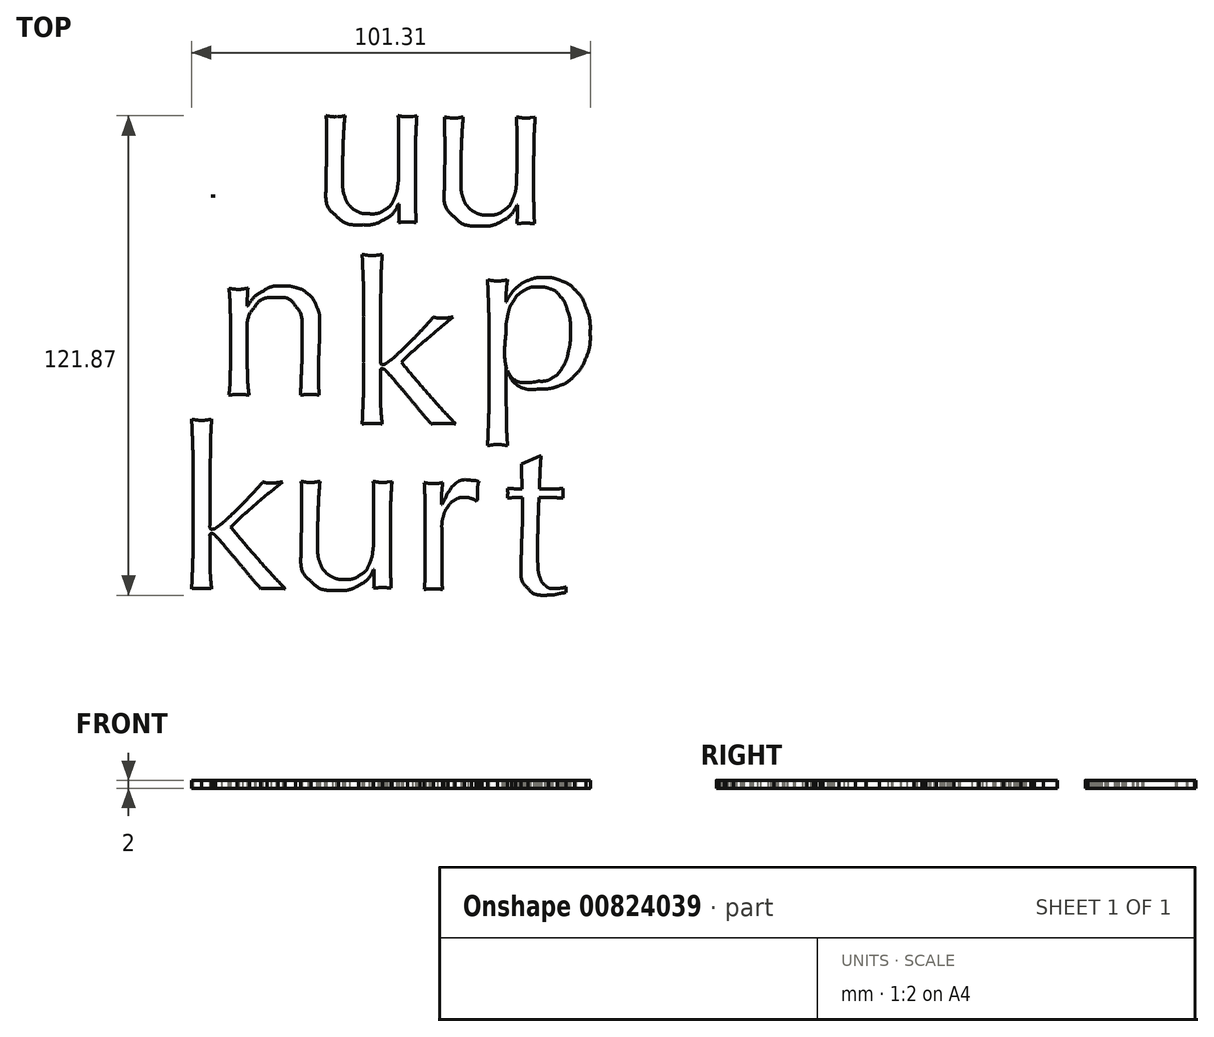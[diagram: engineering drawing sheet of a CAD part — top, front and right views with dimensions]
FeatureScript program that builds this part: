
annotation { "Feature Type Name" : "Feature", "Feature Type Description" : "" }
export const myFeature = defineFeature(function(context is Context, id is Id, definition is map)
    precondition{}
    {
        {
            var Q0;
            Q0=qCreatedBy(makeId("Top.planeOp"),FACE);
            var sketch = newSketch(context, id + "F0", { "sketchPlane" : qUnion([Q0])});
            skFitSpline(sketch, "E0", {"points": [v(-42.87, 37.01) * mm, v(-41.88, 37.01) * mm, v(-40.85, 37) * mm, v(-39.78, 36.95) * mm]});
            skFitSpline(sketch, "E1", {"points": [v(-39.78, 36.95) * mm, v(-38.71, 36.91) * mm, v(-37.69, 36.9) * mm, v(-36.7, 36.9) * mm]});
            skFitSpline(sketch, "E2", {"points": [v(-36.7, 36.9) * mm, v(-35.63, 36.9) * mm, v(-34.56, 36.9) * mm, v(-33.5, 36.9) * mm]});
            skFitSpline(sketch, "E3", {"points": [v(-33.5, 36.9) * mm, v(-32.43, 36.93) * mm, v(-31.36, 36.97) * mm, v(-30.3, 37.01) * mm]});
            skFitSpline(sketch, "E4", {"points": [v(-17.55, 19.24) * mm, v(-18.09, 19.31) * mm, v(-18.6, 19.35) * mm, v(-19.1, 19.35) * mm]});
            skFitSpline(sketch, "E5", {"points": [v(-19.1, 19.35) * mm, v(-19.55, 19.35) * mm, v(-20.05, 19.35) * mm, v(-20.58, 19.35) * mm]});
            skFitSpline(sketch, "E6", {"points": [v(-20.58, 19.35) * mm, v(-21.11, 19.35) * mm, v(-21.63, 19.35) * mm, v(-22.12, 19.35) * mm]});
            skFitSpline(sketch, "E7", {"points": [v(-22.12, 19.35) * mm, v(-22.58, 19.35) * mm, v(-23.08, 19.31) * mm, v(-23.6, 19.24) * mm]});
            skFitSpline(sketch, "E8", {"points": [v(-23.6, 19.24) * mm, v(-23.88, 20.11) * mm, v(-24.24, 21.16) * mm, v(-24.7, 22.38) * mm]});
            skFitSpline(sketch, "E9", {"points": [v(-24.7, 22.38) * mm, v(-25.15, 23.64) * mm, v(-25.67, 24.93) * mm, v(-26.24, 26.27) * mm]});
            skFitSpline(sketch, "E10", {"points": [v(-26.24, 26.27) * mm, v(-26.77, 27.64) * mm, v(-27.32, 29.01) * mm, v(-27.9, 30.38) * mm]});
            skFitSpline(sketch, "E11", {"points": [v(-27.9, 30.38) * mm, v(-28.47, 31.8) * mm, v(-29, 33.12) * mm, v(-29.5, 34.38) * mm]});
            skFitSpline(sketch, "E12", {"points": [v(-29.5, 34.38) * mm, v(-30.71, 34.42) * mm, v(-31.95, 34.44) * mm, v(-33.2, 34.44) * mm]});
            skFitSpline(sketch, "E13", {"points": [v(-33.2, 34.44) * mm, v(-34.47, 34.48) * mm, v(-35.72, 34.5) * mm, v(-36.98, 34.5) * mm]});
            skFitSpline(sketch, "E14", {"points": [v(-36.98, 34.5) * mm, v(-38.16, 34.5) * mm, v(-39.32, 34.48) * mm, v(-40.47, 34.44) * mm]});
            skFitSpline(sketch, "E15", {"points": [v(-40.47, 34.44) * mm, v(-41.6, 34.44) * mm, v(-42.77, 34.42) * mm, v(-43.95, 34.38) * mm]});
            skFitSpline(sketch, "E16", {"points": [v(-43.95, 34.38) * mm, v(-45.17, 31.41) * mm, v(-46.28, 28.57) * mm, v(-47.27, 25.87) * mm]});
            skFitSpline(sketch, "E17", {"points": [v(-47.27, 25.87) * mm, v(-48.26, 23.2) * mm, v(-49, 21) * mm, v(-49.5, 19.24) * mm]});
            skFitSpline(sketch, "E18", {"points": [v(-49.5, 19.24) * mm, v(-50.14, 19.31) * mm, v(-50.85, 19.35) * mm, v(-51.6, 19.35) * mm]});
            skFitSpline(sketch, "E19", {"points": [v(-51.6, 19.35) * mm, v(-52.37, 19.35) * mm, v(-53.08, 19.31) * mm, v(-53.72, 19.24) * mm]});
            skFitSpline(sketch, "E20", {"points": [v(-53.72, 19.24) * mm, v(-50.64, 25.9) * mm, v(-47.63, 32.53) * mm, v(-44.7, 39.12) * mm]});
            skFitSpline(sketch, "E21", {"points": [v(-44.7, 39.12) * mm, v(-41.76, 45.71) * mm, v(-38.8, 52.42) * mm, v(-35.84, 59.24) * mm]});
            skLineSegment(sketch, "E22", {"start": v(-30.3, 37.01) * mm, "end": v(-36.64, 51.52) * mm});
            skLineSegment(sketch, "E23", {"start": v(-36.64, 51.52) * mm, "end": v(-42.87, 37.01) * mm});
            skLineSegment(sketch, "E24", {"start": v(-42.87, 37.01) * mm, "end": v(-30.3, 37.01) * mm});
            skFitSpline(sketch, "E25", {"points": [v(-34.75, 59.24) * mm, v(-33.84, 57.03) * mm, v(-32.85, 54.63) * mm, v(-31.78, 52.04) * mm]});
            skFitSpline(sketch, "E26", {"points": [v(-31.78, 52.04) * mm, v(-30.71, 49.49) * mm, v(-29.63, 46.9) * mm, v(-28.52, 44.27) * mm]});
            skFitSpline(sketch, "E27", {"points": [v(-28.52, 44.27) * mm, v(-27.42, 41.64) * mm, v(-26.31, 39.03) * mm, v(-25.2, 36.44) * mm]});
            skFitSpline(sketch, "E28", {"points": [v(-25.2, 36.44) * mm, v(-24.1, 33.85) * mm, v(-23.08, 31.43) * mm, v(-22.12, 29.18) * mm]});
            skFitSpline(sketch, "E29", {"points": [v(-22.12, 29.18) * mm, v(-21.13, 26.97) * mm, v(-20.26, 25) * mm, v(-19.5, 23.24) * mm]});
            skFitSpline(sketch, "E30", {"points": [v(-19.5, 23.24) * mm, v(-18.7, 21.49) * mm, v(-18.05, 20.15) * mm, v(-17.55, 19.24) * mm]});
            skLineSegment(sketch, "E31", {"start": v(-35.84, 59.24) * mm, "end": v(-34.75, 59.24) * mm});
            skLineSegment(sketch, "E32", {"start": v(-34.75, 59.24) * mm, "end": v(-35.84, 59.24) * mm});
            skFitSpline(sketch, "E33", {"points": [v(-4.04, -4.63) * mm, v(-4.04, -5.93) * mm, v(-4.06, -7.34) * mm, v(-4.1, -8.86) * mm]});
            skFitSpline(sketch, "E34", {"points": [v(-4.1, -8.86) * mm, v(-4.1, -10.39) * mm, v(-4.12, -11.9) * mm, v(-4.16, -13.38) * mm]});
            skFitSpline(sketch, "E35", {"points": [v(-4.16, -13.38) * mm, v(-4.2, -14.86) * mm, v(-4.25, -16.27) * mm, v(-4.33, -17.6) * mm]});
            skFitSpline(sketch, "E36", {"points": [v(-4.33, -17.6) * mm, v(-4.37, -18.94) * mm, v(-4.42, -20.04) * mm, v(-4.5, -20.92) * mm]});
            skFitSpline(sketch, "E37", {"points": [v(-4.5, -20.92) * mm, v(-3.62, -20.84) * mm, v(-2.77, -20.8) * mm, v(-1.93, -20.8) * mm]});
            skFitSpline(sketch, "E38", {"points": [v(-1.93, -20.8) * mm, v(-1.09, -20.8) * mm, v(-0.23, -20.84) * mm, v(0.64, -20.92) * mm]});
            skFitSpline(sketch, "E39", {"points": [v(0.64, -20.92) * mm, v(0.45, -19.28) * mm, v(0.32, -17.66) * mm, v(0.24, -16.06) * mm]});
            skFitSpline(sketch, "E40", {"points": [v(0.24, -16.06) * mm, v(0.2, -14.42) * mm, v(0.19, -12.75) * mm, v(0.19, -11.03) * mm]});
            skLineSegment(sketch, "E41", {"start": v(-4.04, 5.7) * mm, "end": v(-4.04, -4.63) * mm});
            skLineSegment(sketch, "E42", {"start": v(-4.04, -4.63) * mm, "end": v(-4.04, 5.7) * mm});
            skFitSpline(sketch, "E43", {"points": [v(0.19, -7.6) * mm, v(0.19, -7.15) * mm, v(0.38, -6.92) * mm, v(0.76, -6.92) * mm]});
            skFitSpline(sketch, "E44", {"points": [v(0.76, -6.92) * mm, v(0.91, -6.92) * mm, v(1.06, -6.98) * mm, v(1.22, -7.1) * mm]});
            skFitSpline(sketch, "E45", {"points": [v(1.22, -7.1) * mm, v(1.37, -7.2) * mm, v(1.5, -7.34) * mm, v(1.62, -7.5) * mm]});
            skFitSpline(sketch, "E46", {"points": [v(1.62, -7.5) * mm, v(2.3, -8.21) * mm, v(3.12, -9.13) * mm, v(4.07, -10.23) * mm]});
            skFitSpline(sketch, "E47", {"points": [v(4.07, -10.23) * mm, v(5.02, -11.34) * mm, v(6.02, -12.52) * mm, v(7.04, -13.78) * mm]});
            skFitSpline(sketch, "E48", {"points": [v(7.04, -13.78) * mm, v(8.11, -15.03) * mm, v(9.18, -16.31) * mm, v(10.24, -17.6) * mm]});
            skFitSpline(sketch, "E49", {"points": [v(10.24, -17.6) * mm, v(11.31, -18.86) * mm, v(12.26, -19.97) * mm, v(13.1, -20.92) * mm]});
            skFitSpline(sketch, "E50", {"points": [v(13.1, -20.92) * mm, v(13.63, -20.84) * mm, v(14.15, -20.8) * mm, v(14.64, -20.8) * mm]});
            skFitSpline(sketch, "E51", {"points": [v(14.64, -20.8) * mm, v(15.14, -20.8) * mm, v(15.6, -20.8) * mm, v(16.02, -20.8) * mm]});
            skFitSpline(sketch, "E52", {"points": [v(16.02, -20.8) * mm, v(16.51, -20.8) * mm, v(17, -20.8) * mm, v(17.5, -20.8) * mm]});
            skFitSpline(sketch, "E53", {"points": [v(17.5, -20.8) * mm, v(18.03, -20.8) * mm, v(18.62, -20.84) * mm, v(19.27, -20.92) * mm]});
            skFitSpline(sketch, "E54", {"points": [v(19.27, -20.92) * mm, v(16.87, -18.37) * mm, v(14.51, -15.78) * mm, v(12.19, -13.15) * mm]});
            skFitSpline(sketch, "E55", {"points": [v(12.19, -13.15) * mm, v(9.9, -10.52) * mm, v(7.67, -7.9) * mm, v(5.5, -5.26) * mm]});
            skFitSpline(sketch, "E56", {"points": [v(5.5, -5.26) * mm, v(7.48, -3.32) * mm, v(9.56, -1.41) * mm, v(11.73, 0.45) * mm]});
            skFitSpline(sketch, "E57", {"points": [v(11.73, 0.45) * mm, v(13.94, 2.36) * mm, v(16.24, 4.28) * mm, v(18.64, 6.22) * mm]});
            skFitSpline(sketch, "E58", {"points": [v(18.64, 6.22) * mm, v(18, 6.15) * mm, v(17.46, 6.07) * mm, v(17.04, 6) * mm]});
            skFitSpline(sketch, "E59", {"points": [v(17.04, 6) * mm, v(16.62, 5.96) * mm, v(16.2, 5.94) * mm, v(15.79, 5.94) * mm]});
            skFitSpline(sketch, "E60", {"points": [v(15.79, 5.94) * mm, v(15.1, 5.94) * mm, v(14.38, 6.03) * mm, v(13.62, 6.22) * mm]});
            skFitSpline(sketch, "E61", {"points": [v(13.62, 6.22) * mm, v(12.74, 5.2) * mm, v(11.77, 4.1) * mm, v(10.7, 2.97) * mm]});
            skFitSpline(sketch, "E62", {"points": [v(10.7, 2.97) * mm, v(9.63, 1.82) * mm, v(8.59, 0.74) * mm, v(7.56, -0.3) * mm]});
            skFitSpline(sketch, "E63", {"points": [v(7.56, -0.3) * mm, v(6.57, -1.28) * mm, v(5.65, -2.16) * mm, v(4.82, -2.92) * mm]});
            skFitSpline(sketch, "E64", {"points": [v(4.82, -2.92) * mm, v(4.02, -3.68) * mm, v(3.44, -4.2) * mm, v(3.1, -4.46) * mm]});
            skFitSpline(sketch, "E65", {"points": [v(3.1, -4.46) * mm, v(2.64, -4.8) * mm, v(2.22, -5.11) * mm, v(1.84, -5.38) * mm]});
            skFitSpline(sketch, "E66", {"points": [v(1.84, -5.38) * mm, v(1.5, -5.64) * mm, v(1.18, -5.78) * mm, v(0.87, -5.78) * mm]});
            skFitSpline(sketch, "E67", {"points": [v(0.87, -5.78) * mm, v(0.42, -5.78) * mm, v(0.19, -5.41) * mm, v(0.19, -4.7) * mm]});
            skLineSegment(sketch, "E68", {"start": v(0.19, -11.03) * mm, "end": v(0.19, -7.6) * mm});
            skLineSegment(sketch, "E69", {"start": v(0.19, -7.6) * mm, "end": v(0.19, -11.03) * mm});
            skFitSpline(sketch, "E70", {"points": [v(0.19, 5.7) * mm, v(0.19, 7) * mm, v(0.19, 8.41) * mm, v(0.19, 9.94) * mm]});
            skFitSpline(sketch, "E71", {"points": [v(0.19, 9.94) * mm, v(0.22, 11.46) * mm, v(0.26, 12.97) * mm, v(0.3, 14.45) * mm]});
            skFitSpline(sketch, "E72", {"points": [v(0.3, 14.45) * mm, v(0.34, 15.94) * mm, v(0.38, 17.35) * mm, v(0.42, 18.68) * mm]});
            skFitSpline(sketch, "E73", {"points": [v(0.42, 18.68) * mm, v(0.5, 20.05) * mm, v(0.57, 21.21) * mm, v(0.64, 22.17) * mm]});
            skFitSpline(sketch, "E74", {"points": [v(0.64, 22.17) * mm, v(-0.42, 21.98) * mm, v(-1.28, 21.88) * mm, v(-1.93, 21.88) * mm]});
            skFitSpline(sketch, "E75", {"points": [v(-1.93, 21.88) * mm, v(-2.58, 21.88) * mm, v(-3.43, 21.98) * mm, v(-4.5, 22.17) * mm]});
            skFitSpline(sketch, "E76", {"points": [v(-4.5, 22.17) * mm, v(-4.42, 21.21) * mm, v(-4.37, 20.05) * mm, v(-4.33, 18.68) * mm]});
            skFitSpline(sketch, "E77", {"points": [v(-4.33, 18.68) * mm, v(-4.25, 17.35) * mm, v(-4.2, 15.94) * mm, v(-4.16, 14.45) * mm]});
            skFitSpline(sketch, "E78", {"points": [v(-4.16, 14.45) * mm, v(-4.12, 12.97) * mm, v(-4.1, 11.46) * mm, v(-4.1, 9.94) * mm]});
            skFitSpline(sketch, "E79", {"points": [v(-4.1, 9.94) * mm, v(-4.06, 8.41) * mm, v(-4.04, 7) * mm, v(-4.04, 5.7) * mm]});
            skLineSegment(sketch, "E80", {"start": v(0.19, -4.7) * mm, "end": v(0.19, 5.7) * mm});
            skLineSegment(sketch, "E81", {"start": v(0.19, 5.7) * mm, "end": v(0.19, -4.7) * mm});
            skFitSpline(sketch, "E82", {"points": [v(-13.65, 38.87) * mm, v(-13.65, 35.9) * mm, v(-12.8, 33.62) * mm, v(-11.13, 32.02) * mm]});
            skFitSpline(sketch, "E83", {"points": [v(-11.13, 32.02) * mm, v(-9.42, 30.46) * mm, v(-7.07, 29.67) * mm, v(-4.1, 29.67) * mm]});
            skFitSpline(sketch, "E84", {"points": [v(-4.1, 29.67) * mm, v(-2.27, 29.67) * mm, v(-0.58, 30.1) * mm, v(0.98, 30.93) * mm]});
            skFitSpline(sketch, "E85", {"points": [v(0.98, 30.93) * mm, v(2.55, 31.8) * mm, v(3.82, 33.16) * mm, v(4.81, 34.99) * mm]});
            skFitSpline(sketch, "E86", {"points": [v(4.93, 32.53) * mm, v(4.93, 32.11) * mm, v(4.9, 31.71) * mm, v(4.87, 31.33) * mm]});
            skFitSpline(sketch, "E87", {"points": [v(4.87, 31.33) * mm, v(4.87, 30.95) * mm, v(4.85, 30.59) * mm, v(4.81, 30.25) * mm]});
            skFitSpline(sketch, "E88", {"points": [v(4.81, 30.25) * mm, v(5.57, 30.32) * mm, v(6.32, 30.36) * mm, v(7.04, 30.36) * mm]});
            skFitSpline(sketch, "E89", {"points": [v(7.04, 30.36) * mm, v(7.76, 30.36) * mm, v(8.5, 30.32) * mm, v(9.27, 30.25) * mm]});
            skFitSpline(sketch, "E90", {"points": [v(9.27, 30.25) * mm, v(9.2, 31.77) * mm, v(9.14, 33.35) * mm, v(9.1, 34.99) * mm]});
            skFitSpline(sketch, "E91", {"points": [v(9.1, 34.99) * mm, v(9.06, 36.63) * mm, v(9.04, 38.3) * mm, v(9.04, 40.02) * mm]});
            skFitSpline(sketch, "E92", {"points": [v(9.04, 40.02) * mm, v(9.04, 43.1) * mm, v(9.06, 46.02) * mm, v(9.1, 48.76) * mm]});
            skFitSpline(sketch, "E93", {"points": [v(9.1, 48.76) * mm, v(9.14, 51.54) * mm, v(9.25, 54.42) * mm, v(9.44, 57.39) * mm]});
            skFitSpline(sketch, "E94", {"points": [v(9.44, 57.39) * mm, v(9.06, 57.31) * mm, v(8.68, 57.24) * mm, v(8.3, 57.16) * mm]});
            skFitSpline(sketch, "E95", {"points": [v(8.3, 57.16) * mm, v(7.92, 57.12) * mm, v(7.52, 57.1) * mm, v(7.1, 57.1) * mm]});
            skFitSpline(sketch, "E96", {"points": [v(7.1, 57.1) * mm, v(6.68, 57.1) * mm, v(6.28, 57.12) * mm, v(5.9, 57.16) * mm]});
            skFitSpline(sketch, "E97", {"points": [v(5.9, 57.16) * mm, v(5.52, 57.24) * mm, v(5.12, 57.31) * mm, v(4.7, 57.39) * mm]});
            skFitSpline(sketch, "E98", {"points": [v(4.7, 57.39) * mm, v(4.74, 56.7) * mm, v(4.75, 55.98) * mm, v(4.75, 55.22) * mm]});
            skFitSpline(sketch, "E99", {"points": [v(4.75, 55.22) * mm, v(4.8, 54.46) * mm, v(4.81, 53.66) * mm, v(4.81, 52.82) * mm]});
            skLineSegment(sketch, "E100", {"start": v(4.81, 34.99) * mm, "end": v(4.93, 34.99) * mm});
            skLineSegment(sketch, "E101", {"start": v(4.93, 34.99) * mm, "end": v(4.93, 32.53) * mm});
            skLineSegment(sketch, "E102", {"start": v(4.93, 32.53) * mm, "end": v(4.81, 34.99) * mm});
            skFitSpline(sketch, "E103", {"points": [v(4.81, 48.02) * mm, v(4.81, 45.77) * mm, v(4.8, 44) * mm, v(4.75, 42.7) * mm]});
            skFitSpline(sketch, "E104", {"points": [v(4.75, 42.7) * mm, v(4.75, 41.4) * mm, v(4.7, 40.38) * mm, v(4.58, 39.62) * mm]});
            skFitSpline(sketch, "E105", {"points": [v(4.58, 39.62) * mm, v(4.5, 38.86) * mm, v(4.4, 38.25) * mm, v(4.24, 37.79) * mm]});
            skFitSpline(sketch, "E106", {"points": [v(4.24, 37.79) * mm, v(4.09, 37.33) * mm, v(3.88, 36.78) * mm, v(3.61, 36.13) * mm]});
            skFitSpline(sketch, "E107", {"points": [v(3.61, 36.13) * mm, v(3.12, 35.1) * mm, v(2.34, 34.23) * mm, v(1.27, 33.5) * mm]});
            skFitSpline(sketch, "E108", {"points": [v(1.27, 33.5) * mm, v(0.2, 32.82) * mm, v(-1.13, 32.47) * mm, v(-2.73, 32.47) * mm]});
            skFitSpline(sketch, "E109", {"points": [v(-2.73, 32.47) * mm, v(-3.84, 32.47) * mm, v(-4.8, 32.66) * mm, v(-5.65, 33.05) * mm]});
            skFitSpline(sketch, "E110", {"points": [v(-5.65, 33.05) * mm, v(-6.45, 33.46) * mm, v(-7.11, 33.98) * mm, v(-7.65, 34.59) * mm]});
            skFitSpline(sketch, "E111", {"points": [v(-7.65, 34.59) * mm, v(-8.14, 35.12) * mm, v(-8.56, 35.9) * mm, v(-8.9, 36.93) * mm]});
            skFitSpline(sketch, "E112", {"points": [v(-8.9, 36.93) * mm, v(-9.25, 38) * mm, v(-9.42, 39.52) * mm, v(-9.42, 41.5) * mm]});
            skFitSpline(sketch, "E113", {"points": [v(-9.42, 41.5) * mm, v(-9.42, 44.36) * mm, v(-9.38, 47.14) * mm, v(-9.3, 49.85) * mm]});
            skFitSpline(sketch, "E114", {"points": [v(-9.3, 49.85) * mm, v(-9.19, 52.59) * mm, v(-9.04, 55.1) * mm, v(-8.85, 57.39) * mm]});
            skFitSpline(sketch, "E115", {"points": [v(-8.85, 57.39) * mm, v(-9.8, 57.2) * mm, v(-10.58, 57.1) * mm, v(-11.19, 57.1) * mm]});
            skFitSpline(sketch, "E116", {"points": [v(-11.19, 57.1) * mm, v(-11.84, 57.1) * mm, v(-12.64, 57.2) * mm, v(-13.59, 57.39) * mm]});
            skFitSpline(sketch, "E117", {"points": [v(-13.59, 57.39) * mm, v(-13.55, 55.79) * mm, v(-13.53, 54.2) * mm, v(-13.53, 52.65) * mm]});
            skFitSpline(sketch, "E118", {"points": [v(-13.53, 52.65) * mm, v(-13.5, 51.08) * mm, v(-13.47, 49.64) * mm, v(-13.47, 48.3) * mm]});
            skFitSpline(sketch, "E119", {"points": [v(-13.47, 48.3) * mm, v(-13.47, 46.9) * mm, v(-13.51, 45.46) * mm, v(-13.59, 44.02) * mm]});
            skFitSpline(sketch, "E120", {"points": [v(-13.59, 44.02) * mm, v(-13.63, 42.6) * mm, v(-13.65, 40.9) * mm, v(-13.65, 38.87) * mm]});
            skLineSegment(sketch, "E121", {"start": v(4.81, 52.82) * mm, "end": v(4.81, 48.02) * mm});
            skLineSegment(sketch, "E122", {"start": v(4.81, 48.02) * mm, "end": v(4.81, 52.82) * mm});
            skFitSpline(sketch, "E123", {"points": [v(27.8, -10.18) * mm, v(27.8, -11.4) * mm, v(27.79, -12.75) * mm, v(27.75, -14.24) * mm]});
            skFitSpline(sketch, "E124", {"points": [v(27.75, -14.24) * mm, v(27.75, -15.76) * mm, v(27.73, -17.27) * mm, v(27.7, -18.75) * mm]});
            skFitSpline(sketch, "E125", {"points": [v(27.7, -18.75) * mm, v(27.65, -20.24) * mm, v(27.6, -21.65) * mm, v(27.52, -22.98) * mm]});
            skFitSpline(sketch, "E126", {"points": [v(27.52, -22.98) * mm, v(27.48, -24.35) * mm, v(27.42, -25.52) * mm, v(27.35, -26.47) * mm]});
            skFitSpline(sketch, "E127", {"points": [v(27.35, -26.47) * mm, v(28.42, -26.28) * mm, v(29.27, -26.18) * mm, v(29.92, -26.18) * mm]});
            skFitSpline(sketch, "E128", {"points": [v(29.92, -26.18) * mm, v(30.57, -26.18) * mm, v(31.42, -26.28) * mm, v(32.5, -26.47) * mm]});
            skFitSpline(sketch, "E129", {"points": [v(32.5, -26.47) * mm, v(32.42, -25.52) * mm, v(32.34, -24.35) * mm, v(32.26, -22.98) * mm]});
            skFitSpline(sketch, "E130", {"points": [v(32.26, -22.98) * mm, v(32.22, -21.65) * mm, v(32.19, -20.24) * mm, v(32.15, -18.75) * mm]});
            skFitSpline(sketch, "E131", {"points": [v(32.15, -18.75) * mm, v(32.11, -17.27) * mm, v(32.07, -15.76) * mm, v(32.03, -14.24) * mm]});
            skFitSpline(sketch, "E132", {"points": [v(32.03, -14.24) * mm, v(32.03, -12.75) * mm, v(32.03, -11.4) * mm, v(32.03, -10.18) * mm]});
            skLineSegment(sketch, "E133", {"start": v(27.8, -0.93) * mm, "end": v(27.8, -10.18) * mm});
            skLineSegment(sketch, "E134", {"start": v(27.8, -10.18) * mm, "end": v(27.8, -0.93) * mm});
            skFitSpline(sketch, "E135", {"points": [v(32.15, -6.58) * mm, v(33.94, -10.2) * mm, v(36.93, -12.01) * mm, v(41.12, -12.01) * mm]});
            skFitSpline(sketch, "E136", {"points": [v(41.12, -12.01) * mm, v(42.6, -12.01) * mm, v(44.1, -11.74) * mm, v(45.58, -11.21) * mm]});
            skFitSpline(sketch, "E137", {"points": [v(45.58, -11.21) * mm, v(47.06, -10.64) * mm, v(48.38, -9.76) * mm, v(49.52, -8.58) * mm]});
            skFitSpline(sketch, "E138", {"points": [v(49.52, -8.58) * mm, v(50.7, -7.4) * mm, v(51.65, -5.92) * mm, v(52.38, -4.13) * mm]});
            skFitSpline(sketch, "E139", {"points": [v(52.38, -4.13) * mm, v(53.1, -2.33) * mm, v(53.46, -0.22) * mm, v(53.46, 2.22) * mm]});
            skFitSpline(sketch, "E140", {"points": [v(53.46, 2.22) * mm, v(53.46, 4.66) * mm, v(53.12, 6.75) * mm, v(52.43, 8.5) * mm]});
            skFitSpline(sketch, "E141", {"points": [v(52.43, 8.5) * mm, v(51.79, 10.3) * mm, v(50.91, 11.76) * mm, v(49.8, 12.9) * mm]});
            skFitSpline(sketch, "E142", {"points": [v(49.8, 12.9) * mm, v(48.74, 14.05) * mm, v(47.5, 14.88) * mm, v(46.1, 15.42) * mm]});
            skFitSpline(sketch, "E143", {"points": [v(46.1, 15.42) * mm, v(44.68, 15.99) * mm, v(43.25, 16.27) * mm, v(41.8, 16.27) * mm]});
            skFitSpline(sketch, "E144", {"points": [v(41.8, 16.27) * mm, v(40.4, 16.27) * mm, v(39.14, 16.07) * mm, v(38.03, 15.65) * mm]});
            skFitSpline(sketch, "E145", {"points": [v(38.03, 15.65) * mm, v(36.93, 15.23) * mm, v(35.98, 14.7) * mm, v(35.18, 14.05) * mm]});
            skFitSpline(sketch, "E146", {"points": [v(35.18, 14.05) * mm, v(34.42, 13.44) * mm, v(33.79, 12.77) * mm, v(33.3, 12.05) * mm]});
            skFitSpline(sketch, "E147", {"points": [v(33.3, 12.05) * mm, v(32.8, 11.36) * mm, v(32.42, 10.71) * mm, v(32.15, 10.1) * mm]});
            skLineSegment(sketch, "E148", {"start": v(32.03, -10.18) * mm, "end": v(32.03, -6.58) * mm});
            skLineSegment(sketch, "E149", {"start": v(32.03, -6.58) * mm, "end": v(32.15, -6.58) * mm});
            skLineSegment(sketch, "E150", {"start": v(32.15, -6.58) * mm, "end": v(32.03, -10.18) * mm});
            skFitSpline(sketch, "E151", {"points": [v(32.03, 10.1) * mm, v(32.03, 11.02) * mm, v(32.07, 11.93) * mm, v(32.15, 12.85) * mm]});
            skFitSpline(sketch, "E152", {"points": [v(32.15, 12.85) * mm, v(32.22, 13.76) * mm, v(32.34, 14.71) * mm, v(32.5, 15.7) * mm]});
            skFitSpline(sketch, "E153", {"points": [v(32.5, 15.7) * mm, v(31.42, 15.51) * mm, v(30.57, 15.42) * mm, v(29.92, 15.42) * mm]});
            skFitSpline(sketch, "E154", {"points": [v(29.92, 15.42) * mm, v(29.27, 15.42) * mm, v(28.42, 15.51) * mm, v(27.35, 15.7) * mm]});
            skFitSpline(sketch, "E155", {"points": [v(27.35, 15.7) * mm, v(27.42, 14.71) * mm, v(27.48, 13.53) * mm, v(27.52, 12.16) * mm]});
            skFitSpline(sketch, "E156", {"points": [v(27.52, 12.16) * mm, v(27.6, 10.79) * mm, v(27.65, 9.34) * mm, v(27.7, 7.82) * mm]});
            skFitSpline(sketch, "E157", {"points": [v(27.7, 7.82) * mm, v(27.73, 6.33) * mm, v(27.75, 4.83) * mm, v(27.75, 3.3) * mm]});
            skFitSpline(sketch, "E158", {"points": [v(27.75, 3.3) * mm, v(27.79, 1.78) * mm, v(27.8, 0.37) * mm, v(27.8, -0.93) * mm]});
            skLineSegment(sketch, "E159", {"start": v(32.15, 10.1) * mm, "end": v(32.03, 10.1) * mm});
            skLineSegment(sketch, "E160", {"start": v(32.03, 10.1) * mm, "end": v(32.15, 10.1) * mm});
            skFitSpline(sketch, "E161", {"points": [v(48.43, 2.27) * mm, v(48.43, 0.56) * mm, v(48.26, -1.06) * mm, v(47.92, -2.58) * mm]});
            skFitSpline(sketch, "E162", {"points": [v(47.92, -2.58) * mm, v(47.62, -4.07) * mm, v(47.12, -5.38) * mm, v(46.43, -6.53) * mm]});
            skFitSpline(sketch, "E163", {"points": [v(46.43, -6.53) * mm, v(45.79, -7.63) * mm, v(44.95, -8.5) * mm, v(43.92, -9.15) * mm]});
            skFitSpline(sketch, "E164", {"points": [v(43.92, -9.15) * mm, v(42.93, -9.76) * mm, v(41.75, -10.07) * mm, v(40.38, -10.07) * mm]});
            skFitSpline(sketch, "E165", {"points": [v(40.38, -10.07) * mm, v(34.82, -10.07) * mm, v(32.03, -6.1) * mm, v(32.03, 1.82) * mm]});
            skFitSpline(sketch, "E166", {"points": [v(32.03, 1.82) * mm, v(32.03, 3.46) * mm, v(32.19, 5) * mm, v(32.5, 6.45) * mm]});
            skFitSpline(sketch, "E167", {"points": [v(32.5, 6.45) * mm, v(32.8, 7.93) * mm, v(33.3, 9.2) * mm, v(33.98, 10.27) * mm]});
            skFitSpline(sketch, "E168", {"points": [v(33.98, 10.27) * mm, v(34.66, 11.38) * mm, v(35.54, 12.26) * mm, v(36.6, 12.9) * mm]});
            skFitSpline(sketch, "E169", {"points": [v(36.6, 12.9) * mm, v(37.71, 13.55) * mm, v(39.02, 13.87) * mm, v(40.55, 13.87) * mm]});
            skFitSpline(sketch, "E170", {"points": [v(40.55, 13.87) * mm, v(41.46, 13.87) * mm, v(42.4, 13.7) * mm, v(43.35, 13.36) * mm]});
            skFitSpline(sketch, "E171", {"points": [v(43.35, 13.36) * mm, v(44.3, 13.02) * mm, v(45.14, 12.39) * mm, v(45.86, 11.47) * mm]});
            skFitSpline(sketch, "E172", {"points": [v(45.86, 11.47) * mm, v(46.62, 10.6) * mm, v(47.23, 9.42) * mm, v(47.7, 7.93) * mm]});
            skFitSpline(sketch, "E173", {"points": [v(47.7, 7.93) * mm, v(48.19, 6.45) * mm, v(48.43, 4.56) * mm, v(48.43, 2.27) * mm]});
            skFitSpline(sketch, "E174", {"points": [v(16.4, 38.57) * mm, v(16.4, 35.6) * mm, v(17.24, 33.32) * mm, v(18.92, 31.72) * mm]});
            skFitSpline(sketch, "E175", {"points": [v(18.92, 31.72) * mm, v(20.64, 30.16) * mm, v(22.98, 29.37) * mm, v(25.95, 29.37) * mm]});
            skFitSpline(sketch, "E176", {"points": [v(25.95, 29.37) * mm, v(27.78, 29.37) * mm, v(29.47, 29.8) * mm, v(31.04, 30.63) * mm]});
            skFitSpline(sketch, "E177", {"points": [v(31.04, 30.63) * mm, v(32.6, 31.5) * mm, v(33.87, 32.86) * mm, v(34.86, 34.69) * mm]});
            skFitSpline(sketch, "E178", {"points": [v(34.98, 32.23) * mm, v(34.98, 31.81) * mm, v(34.96, 31.41) * mm, v(34.92, 31.03) * mm]});
            skFitSpline(sketch, "E179", {"points": [v(34.92, 31.03) * mm, v(34.92, 30.65) * mm, v(34.9, 30.29) * mm, v(34.86, 29.95) * mm]});
            skFitSpline(sketch, "E180", {"points": [v(34.86, 29.95) * mm, v(35.63, 30.02) * mm, v(36.37, 30.06) * mm, v(37.1, 30.06) * mm]});
            skFitSpline(sketch, "E181", {"points": [v(37.1, 30.06) * mm, v(37.82, 30.06) * mm, v(38.56, 30.02) * mm, v(39.32, 29.95) * mm]});
            skFitSpline(sketch, "E182", {"points": [v(39.32, 29.95) * mm, v(39.24, 31.47) * mm, v(39.19, 33.05) * mm, v(39.15, 34.69) * mm]});
            skFitSpline(sketch, "E183", {"points": [v(39.15, 34.69) * mm, v(39.11, 36.33) * mm, v(39.1, 38) * mm, v(39.1, 39.72) * mm]});
            skFitSpline(sketch, "E184", {"points": [v(39.1, 39.72) * mm, v(39.1, 42.8) * mm, v(39.11, 45.72) * mm, v(39.15, 48.46) * mm]});
            skFitSpline(sketch, "E185", {"points": [v(39.15, 48.46) * mm, v(39.19, 51.24) * mm, v(39.3, 54.12) * mm, v(39.5, 57.09) * mm]});
            skFitSpline(sketch, "E186", {"points": [v(39.5, 57.09) * mm, v(39.11, 57.01) * mm, v(38.73, 56.94) * mm, v(38.35, 56.86) * mm]});
            skFitSpline(sketch, "E187", {"points": [v(38.35, 56.86) * mm, v(37.97, 56.82) * mm, v(37.57, 56.8) * mm, v(37.15, 56.8) * mm]});
            skFitSpline(sketch, "E188", {"points": [v(37.15, 56.8) * mm, v(36.73, 56.8) * mm, v(36.33, 56.82) * mm, v(35.95, 56.86) * mm]});
            skFitSpline(sketch, "E189", {"points": [v(35.95, 56.86) * mm, v(35.57, 56.94) * mm, v(35.17, 57.01) * mm, v(34.75, 57.09) * mm]});
            skFitSpline(sketch, "E190", {"points": [v(34.75, 57.09) * mm, v(34.79, 56.4) * mm, v(34.8, 55.68) * mm, v(34.8, 54.92) * mm]});
            skFitSpline(sketch, "E191", {"points": [v(34.8, 54.92) * mm, v(34.84, 54.16) * mm, v(34.86, 53.36) * mm, v(34.86, 52.52) * mm]});
            skLineSegment(sketch, "E192", {"start": v(34.86, 34.69) * mm, "end": v(34.98, 34.69) * mm});
            skLineSegment(sketch, "E193", {"start": v(34.98, 34.69) * mm, "end": v(34.98, 32.23) * mm});
            skLineSegment(sketch, "E194", {"start": v(34.98, 32.23) * mm, "end": v(34.86, 34.69) * mm});
            skFitSpline(sketch, "E195", {"points": [v(34.86, 47.72) * mm, v(34.86, 45.47) * mm, v(34.84, 43.7) * mm, v(34.8, 42.4) * mm]});
            skFitSpline(sketch, "E196", {"points": [v(34.8, 42.4) * mm, v(34.8, 41.1) * mm, v(34.75, 40.08) * mm, v(34.64, 39.32) * mm]});
            skFitSpline(sketch, "E197", {"points": [v(34.64, 39.32) * mm, v(34.56, 38.56) * mm, v(34.44, 37.95) * mm, v(34.3, 37.49) * mm]});
            skFitSpline(sketch, "E198", {"points": [v(34.3, 37.49) * mm, v(34.14, 37.03) * mm, v(33.93, 36.48) * mm, v(33.66, 35.83) * mm]});
            skFitSpline(sketch, "E199", {"points": [v(33.66, 35.83) * mm, v(33.17, 34.8) * mm, v(32.39, 33.93) * mm, v(31.32, 33.2) * mm]});
            skFitSpline(sketch, "E200", {"points": [v(31.32, 33.2) * mm, v(30.25, 32.52) * mm, v(28.92, 32.17) * mm, v(27.32, 32.17) * mm]});
            skFitSpline(sketch, "E201", {"points": [v(27.32, 32.17) * mm, v(26.22, 32.17) * mm, v(25.24, 32.36) * mm, v(24.4, 32.75) * mm]});
            skFitSpline(sketch, "E202", {"points": [v(24.4, 32.75) * mm, v(23.6, 33.16) * mm, v(22.94, 33.68) * mm, v(22.4, 34.29) * mm]});
            skFitSpline(sketch, "E203", {"points": [v(22.4, 34.29) * mm, v(21.91, 34.82) * mm, v(21.5, 35.6) * mm, v(21.15, 36.63) * mm]});
            skFitSpline(sketch, "E204", {"points": [v(21.15, 36.63) * mm, v(20.8, 37.7) * mm, v(20.64, 39.22) * mm, v(20.64, 41.2) * mm]});
            skFitSpline(sketch, "E205", {"points": [v(20.64, 41.2) * mm, v(20.64, 44.06) * mm, v(20.67, 46.84) * mm, v(20.75, 49.55) * mm]});
            skFitSpline(sketch, "E206", {"points": [v(20.75, 49.55) * mm, v(20.86, 52.29) * mm, v(21.02, 54.8) * mm, v(21.2, 57.09) * mm]});
            skFitSpline(sketch, "E207", {"points": [v(21.2, 57.09) * mm, v(20.25, 56.9) * mm, v(19.47, 56.8) * mm, v(18.86, 56.8) * mm]});
            skFitSpline(sketch, "E208", {"points": [v(18.86, 56.8) * mm, v(18.22, 56.8) * mm, v(17.42, 56.9) * mm, v(16.46, 57.09) * mm]});
            skFitSpline(sketch, "E209", {"points": [v(16.46, 57.09) * mm, v(16.5, 55.49) * mm, v(16.52, 53.9) * mm, v(16.52, 52.35) * mm]});
            skFitSpline(sketch, "E210", {"points": [v(16.52, 52.35) * mm, v(16.56, 50.78) * mm, v(16.58, 49.34) * mm, v(16.58, 48) * mm]});
            skFitSpline(sketch, "E211", {"points": [v(16.58, 48) * mm, v(16.58, 46.6) * mm, v(16.54, 45.16) * mm, v(16.46, 43.72) * mm]});
            skFitSpline(sketch, "E212", {"points": [v(16.46, 43.72) * mm, v(16.43, 42.3) * mm, v(16.4, 40.6) * mm, v(16.4, 38.57) * mm]});
            skLineSegment(sketch, "E213", {"start": v(34.86, 52.52) * mm, "end": v(34.86, 47.72) * mm});
            skLineSegment(sketch, "E214", {"start": v(34.86, 47.72) * mm, "end": v(34.86, 52.52) * mm});
            skFitSpline(sketch, "E215", {"points": [v(-19.71, -1.02) * mm, v(-19.71, -3.23) * mm, v(-19.77, -5.38) * mm, v(-19.88, -7.47) * mm]});
            skFitSpline(sketch, "E216", {"points": [v(-19.88, -7.47) * mm, v(-19.96, -9.57) * mm, v(-20.04, -11.6) * mm, v(-20.11, -13.59) * mm]});
            skFitSpline(sketch, "E217", {"points": [v(-20.11, -13.59) * mm, v(-19.35, -13.51) * mm, v(-18.57, -13.47) * mm, v(-17.77, -13.47) * mm]});
            skFitSpline(sketch, "E218", {"points": [v(-17.77, -13.47) * mm, v(-16.93, -13.47) * mm, v(-16.13, -13.51) * mm, v(-15.37, -13.59) * mm]});
            skFitSpline(sketch, "E219", {"points": [v(-15.37, -13.59) * mm, v(-15.4, -13.05) * mm, v(-15.45, -12.5) * mm, v(-15.48, -11.93) * mm]});
            skFitSpline(sketch, "E220", {"points": [v(-15.48, -11.93) * mm, v(-15.48, -11.32) * mm, v(-15.48, -10.71) * mm, v(-15.48, -10.1) * mm]});
            skLineSegment(sketch, "E221", {"start": v(-19.71, 2.47) * mm, "end": v(-19.71, -1.02) * mm});
            skLineSegment(sketch, "E222", {"start": v(-19.71, -1.02) * mm, "end": v(-19.71, 2.47) * mm});
            skFitSpline(sketch, "E223", {"points": [v(-15.48, -6.39) * mm, v(-15.48, -4.44) * mm, v(-15.45, -2.62) * mm, v(-15.37, -0.9) * mm]});
            skFitSpline(sketch, "E224", {"points": [v(-15.37, -0.9) * mm, v(-15.3, 0.85) * mm, v(-15.25, 2.55) * mm, v(-15.25, 4.18) * mm]});
            skFitSpline(sketch, "E225", {"points": [v(-15.25, 4.18) * mm, v(-15.25, 6.17) * mm, v(-15.54, 7.78) * mm, v(-16.11, 9.04) * mm]});
            skFitSpline(sketch, "E226", {"points": [v(-16.11, 9.04) * mm, v(-16.65, 10.34) * mm, v(-17.35, 11.35) * mm, v(-18.23, 12.07) * mm]});
            skFitSpline(sketch, "E227", {"points": [v(-18.23, 12.07) * mm, v(-19.1, 12.83) * mm, v(-20.1, 13.37) * mm, v(-21.2, 13.67) * mm]});
            skFitSpline(sketch, "E228", {"points": [v(-21.2, 13.67) * mm, v(-22.26, 13.97) * mm, v(-23.33, 14.13) * mm, v(-24.4, 14.13) * mm]});
            skFitSpline(sketch, "E229", {"points": [v(-24.4, 14.13) * mm, v(-26.45, 14.13) * mm, v(-28.23, 13.67) * mm, v(-29.71, 12.76) * mm]});
            skFitSpline(sketch, "E230", {"points": [v(-29.71, 12.76) * mm, v(-31.2, 11.88) * mm, v(-32.47, 10.62) * mm, v(-33.54, 8.98) * mm]});
            skLineSegment(sketch, "E231", {"start": v(-15.48, -10.1) * mm, "end": v(-15.48, -6.39) * mm});
            skLineSegment(sketch, "E232", {"start": v(-15.48, -6.39) * mm, "end": v(-15.48, -10.1) * mm});
            skFitSpline(sketch, "E233", {"points": [v(-33.65, 8.98) * mm, v(-33.65, 10.5) * mm, v(-33.6, 12.03) * mm, v(-33.48, 13.56) * mm]});
            skFitSpline(sketch, "E234", {"points": [v(-33.48, 13.56) * mm, v(-33.98, 13.48) * mm, v(-34.42, 13.4) * mm, v(-34.8, 13.33) * mm]});
            skFitSpline(sketch, "E235", {"points": [v(-34.8, 13.33) * mm, v(-35.14, 13.29) * mm, v(-35.46, 13.27) * mm, v(-35.77, 13.27) * mm]});
            skFitSpline(sketch, "E236", {"points": [v(-35.77, 13.27) * mm, v(-36.42, 13.27) * mm, v(-37.27, 13.37) * mm, v(-38.34, 13.56) * mm]});
            skFitSpline(sketch, "E237", {"points": [v(-38.34, 13.56) * mm, v(-38.15, 11.92) * mm, v(-38.04, 10.15) * mm, v(-38, 8.24) * mm]});
            skFitSpline(sketch, "E238", {"points": [v(-38, 8.24) * mm, v(-37.92, 6.37) * mm, v(-37.88, 4.58) * mm, v(-37.88, 2.87) * mm]});
            skLineSegment(sketch, "E239", {"start": v(-33.54, 8.98) * mm, "end": v(-33.65, 8.98) * mm});
            skLineSegment(sketch, "E240", {"start": v(-33.65, 8.98) * mm, "end": v(-33.54, 8.98) * mm});
            skFitSpline(sketch, "E241", {"points": [v(-37.88, -3.07) * mm, v(-37.88, -4.79) * mm, v(-37.92, -6.6) * mm, v(-38, -8.5) * mm]});
            skFitSpline(sketch, "E242", {"points": [v(-38, -8.5) * mm, v(-38.04, -10.37) * mm, v(-38.15, -12.06) * mm, v(-38.34, -13.59) * mm]});
            skFitSpline(sketch, "E243", {"points": [v(-38.34, -13.59) * mm, v(-37.46, -13.51) * mm, v(-36.6, -13.47) * mm, v(-35.77, -13.47) * mm]});
            skFitSpline(sketch, "E244", {"points": [v(-35.77, -13.47) * mm, v(-34.93, -13.47) * mm, v(-34.07, -13.51) * mm, v(-33.2, -13.59) * mm]});
            skFitSpline(sketch, "E245", {"points": [v(-33.2, -13.59) * mm, v(-33.39, -12.06) * mm, v(-33.52, -10.37) * mm, v(-33.6, -8.5) * mm]});
            skFitSpline(sketch, "E246", {"points": [v(-33.6, -8.5) * mm, v(-33.64, -6.6) * mm, v(-33.65, -4.79) * mm, v(-33.65, -3.07) * mm]});
            skLineSegment(sketch, "E247", {"start": v(-37.88, 2.87) * mm, "end": v(-37.88, -3.07) * mm});
            skLineSegment(sketch, "E248", {"start": v(-37.88, -3.07) * mm, "end": v(-37.88, 2.87) * mm});
            skFitSpline(sketch, "E249", {"points": [v(-33.65, 1.78) * mm, v(-33.65, 4.76) * mm, v(-33.05, 7.06) * mm, v(-31.83, 8.7) * mm]});
            skFitSpline(sketch, "E250", {"points": [v(-31.83, 8.7) * mm, v(-30.57, 10.34) * mm, v(-28.6, 11.16) * mm, v(-25.94, 11.16) * mm]});
            skFitSpline(sketch, "E251", {"points": [v(-25.94, 11.16) * mm, v(-24, 11.16) * mm, v(-22.47, 10.41) * mm, v(-21.37, 8.93) * mm]});
            skFitSpline(sketch, "E252", {"points": [v(-21.37, 8.93) * mm, v(-20.26, 7.48) * mm, v(-19.71, 5.33) * mm, v(-19.71, 2.47) * mm]});
            skLineSegment(sketch, "E253", {"start": v(-33.65, -3.07) * mm, "end": v(-33.65, 1.78) * mm});
            skLineSegment(sketch, "E254", {"start": v(-33.65, 1.78) * mm, "end": v(-33.65, -3.07) * mm});
            skFitSpline(sketch, "E255", {"points": [v(-47.37, -46.52) * mm, v(-47.37, -47.81) * mm, v(-47.39, -49.22) * mm, v(-47.42, -50.74) * mm]});
            skFitSpline(sketch, "E256", {"points": [v(-47.42, -50.74) * mm, v(-47.42, -52.27) * mm, v(-47.44, -53.77) * mm, v(-47.48, -55.26) * mm]});
            skFitSpline(sketch, "E257", {"points": [v(-47.48, -55.26) * mm, v(-47.52, -56.74) * mm, v(-47.58, -58.15) * mm, v(-47.65, -59.49) * mm]});
            skFitSpline(sketch, "E258", {"points": [v(-47.65, -59.49) * mm, v(-47.69, -60.82) * mm, v(-47.75, -61.93) * mm, v(-47.82, -62.8) * mm]});
            skFitSpline(sketch, "E259", {"points": [v(-47.82, -62.8) * mm, v(-46.95, -62.73) * mm, v(-46.09, -62.69) * mm, v(-45.25, -62.69) * mm]});
            skFitSpline(sketch, "E260", {"points": [v(-45.25, -62.69) * mm, v(-44.41, -62.69) * mm, v(-43.56, -62.73) * mm, v(-42.68, -62.8) * mm]});
            skFitSpline(sketch, "E261", {"points": [v(-42.68, -62.8) * mm, v(-42.87, -61.16) * mm, v(-43, -59.54) * mm, v(-43.08, -57.94) * mm]});
            skFitSpline(sketch, "E262", {"points": [v(-43.08, -57.94) * mm, v(-43.12, -56.3) * mm, v(-43.14, -54.63) * mm, v(-43.14, -52.92) * mm]});
            skLineSegment(sketch, "E263", {"start": v(-47.37, -36.17) * mm, "end": v(-47.37, -46.52) * mm});
            skLineSegment(sketch, "E264", {"start": v(-47.37, -46.52) * mm, "end": v(-47.37, -36.17) * mm});
            skFitSpline(sketch, "E265", {"points": [v(-43.14, -49.49) * mm, v(-43.14, -49.03) * mm, v(-42.95, -48.8) * mm, v(-42.57, -48.8) * mm]});
            skFitSpline(sketch, "E266", {"points": [v(-42.57, -48.8) * mm, v(-42.41, -48.8) * mm, v(-42.26, -48.86) * mm, v(-42.1, -48.97) * mm]});
            skFitSpline(sketch, "E267", {"points": [v(-42.1, -48.97) * mm, v(-41.96, -49.09) * mm, v(-41.82, -49.22) * mm, v(-41.7, -49.37) * mm]});
            skFitSpline(sketch, "E268", {"points": [v(-41.7, -49.37) * mm, v(-41.02, -50.1) * mm, v(-40.2, -51.01) * mm, v(-39.25, -52.12) * mm]});
            skFitSpline(sketch, "E269", {"points": [v(-39.25, -52.12) * mm, v(-38.3, -53.22) * mm, v(-37.3, -54.4) * mm, v(-36.28, -55.66) * mm]});
            skFitSpline(sketch, "E270", {"points": [v(-36.28, -55.66) * mm, v(-35.21, -56.92) * mm, v(-34.15, -58.2) * mm, v(-33.08, -59.49) * mm]});
            skFitSpline(sketch, "E271", {"points": [v(-33.08, -59.49) * mm, v(-32.01, -60.74) * mm, v(-31.06, -61.85) * mm, v(-30.22, -62.8) * mm]});
            skFitSpline(sketch, "E272", {"points": [v(-30.22, -62.8) * mm, v(-29.69, -62.73) * mm, v(-29.18, -62.69) * mm, v(-28.68, -62.69) * mm]});
            skFitSpline(sketch, "E273", {"points": [v(-28.68, -62.69) * mm, v(-28.19, -62.69) * mm, v(-27.73, -62.69) * mm, v(-27.3, -62.69) * mm]});
            skFitSpline(sketch, "E274", {"points": [v(-27.3, -62.69) * mm, v(-26.81, -62.69) * mm, v(-26.32, -62.69) * mm, v(-25.82, -62.69) * mm]});
            skFitSpline(sketch, "E275", {"points": [v(-25.82, -62.69) * mm, v(-25.29, -62.69) * mm, v(-24.7, -62.73) * mm, v(-24.05, -62.8) * mm]});
            skFitSpline(sketch, "E276", {"points": [v(-24.05, -62.8) * mm, v(-26.45, -60.25) * mm, v(-28.81, -57.66) * mm, v(-31.14, -55.03) * mm]});
            skFitSpline(sketch, "E277", {"points": [v(-31.14, -55.03) * mm, v(-33.42, -52.4) * mm, v(-35.65, -49.77) * mm, v(-37.82, -47.14) * mm]});
            skFitSpline(sketch, "E278", {"points": [v(-37.82, -47.14) * mm, v(-35.84, -45.2) * mm, v(-33.77, -43.3) * mm, v(-31.6, -41.43) * mm]});
            skFitSpline(sketch, "E279", {"points": [v(-31.6, -41.43) * mm, v(-29.39, -39.53) * mm, v(-27.08, -37.6) * mm, v(-24.68, -35.66) * mm]});
            skFitSpline(sketch, "E280", {"points": [v(-24.68, -35.66) * mm, v(-25.33, -35.74) * mm, v(-25.86, -35.81) * mm, v(-26.28, -35.89) * mm]});
            skFitSpline(sketch, "E281", {"points": [v(-26.28, -35.89) * mm, v(-26.7, -35.93) * mm, v(-27.12, -35.94) * mm, v(-27.54, -35.94) * mm]});
            skFitSpline(sketch, "E282", {"points": [v(-27.54, -35.94) * mm, v(-28.22, -35.94) * mm, v(-28.95, -35.85) * mm, v(-29.7, -35.66) * mm]});
            skFitSpline(sketch, "E283", {"points": [v(-29.7, -35.66) * mm, v(-30.59, -36.69) * mm, v(-31.56, -37.77) * mm, v(-32.62, -38.92) * mm]});
            skFitSpline(sketch, "E284", {"points": [v(-32.62, -38.92) * mm, v(-33.69, -40.06) * mm, v(-34.74, -41.14) * mm, v(-35.77, -42.17) * mm]});
            skFitSpline(sketch, "E285", {"points": [v(-35.77, -42.17) * mm, v(-36.76, -43.16) * mm, v(-37.67, -44.04) * mm, v(-38.5, -44.8) * mm]});
            skFitSpline(sketch, "E286", {"points": [v(-38.5, -44.8) * mm, v(-39.3, -45.56) * mm, v(-39.88, -46.08) * mm, v(-40.22, -46.34) * mm]});
            skFitSpline(sketch, "E287", {"points": [v(-40.22, -46.34) * mm, v(-40.68, -46.69) * mm, v(-41.1, -47) * mm, v(-41.48, -47.26) * mm]});
            skFitSpline(sketch, "E288", {"points": [v(-41.48, -47.26) * mm, v(-41.82, -47.53) * mm, v(-42.15, -47.66) * mm, v(-42.45, -47.66) * mm]});
            skFitSpline(sketch, "E289", {"points": [v(-42.45, -47.66) * mm, v(-42.9, -47.66) * mm, v(-43.14, -47.3) * mm, v(-43.14, -46.57) * mm]});
            skLineSegment(sketch, "E290", {"start": v(-43.14, -52.92) * mm, "end": v(-43.14, -49.49) * mm});
            skLineSegment(sketch, "E291", {"start": v(-43.14, -49.49) * mm, "end": v(-43.14, -52.92) * mm});
            skFitSpline(sketch, "E292", {"points": [v(-43.14, -36.17) * mm, v(-43.14, -34.88) * mm, v(-43.14, -33.47) * mm, v(-43.14, -31.94) * mm]});
            skFitSpline(sketch, "E293", {"points": [v(-43.14, -31.94) * mm, v(-43.1, -30.42) * mm, v(-43.06, -28.92) * mm, v(-43.02, -27.43) * mm]});
            skFitSpline(sketch, "E294", {"points": [v(-43.02, -27.43) * mm, v(-42.99, -25.94) * mm, v(-42.95, -24.54) * mm, v(-42.9, -23.2) * mm]});
            skFitSpline(sketch, "E295", {"points": [v(-42.9, -23.2) * mm, v(-42.83, -21.83) * mm, v(-42.76, -20.67) * mm, v(-42.68, -19.72) * mm]});
            skFitSpline(sketch, "E296", {"points": [v(-42.68, -19.72) * mm, v(-43.75, -19.9) * mm, v(-44.6, -20) * mm, v(-45.25, -20) * mm]});
            skFitSpline(sketch, "E297", {"points": [v(-45.25, -20) * mm, v(-45.9, -20) * mm, v(-46.76, -19.9) * mm, v(-47.82, -19.72) * mm]});
            skFitSpline(sketch, "E298", {"points": [v(-47.82, -19.72) * mm, v(-47.75, -20.67) * mm, v(-47.69, -21.83) * mm, v(-47.65, -23.2) * mm]});
            skFitSpline(sketch, "E299", {"points": [v(-47.65, -23.2) * mm, v(-47.58, -24.54) * mm, v(-47.52, -25.94) * mm, v(-47.48, -27.43) * mm]});
            skFitSpline(sketch, "E300", {"points": [v(-47.48, -27.43) * mm, v(-47.44, -28.92) * mm, v(-47.42, -30.42) * mm, v(-47.42, -31.94) * mm]});
            skFitSpline(sketch, "E301", {"points": [v(-47.42, -31.94) * mm, v(-47.39, -33.47) * mm, v(-47.37, -34.88) * mm, v(-47.37, -36.17) * mm]});
            skLineSegment(sketch, "E302", {"start": v(-43.14, -46.57) * mm, "end": v(-43.14, -36.17) * mm});
            skLineSegment(sketch, "E303", {"start": v(-43.14, -36.17) * mm, "end": v(-43.14, -46.57) * mm});
            skFitSpline(sketch, "E304", {"points": [v(35.96, -31.05) * mm, v(36.04, -32.27) * mm, v(36.08, -33.45) * mm, v(36.08, -34.6) * mm]});
            skFitSpline(sketch, "E305", {"points": [v(36.08, -34.6) * mm, v(36.11, -35.74) * mm, v(36.15, -36.7) * mm, v(36.2, -37.45) * mm]});
            skFitSpline(sketch, "E306", {"points": [v(36.2, -37.45) * mm, v(35.4, -37.45) * mm, v(34.13, -37.4) * mm, v(32.42, -37.28) * mm]});
            skFitSpline(sketch, "E307", {"points": [v(32.42, -37.28) * mm, v(32.46, -37.47) * mm, v(32.48, -37.66) * mm, v(32.48, -37.85) * mm]});
            skFitSpline(sketch, "E308", {"points": [v(32.48, -37.85) * mm, v(32.51, -38.04) * mm, v(32.53, -38.23) * mm, v(32.53, -38.42) * mm]});
            skFitSpline(sketch, "E309", {"points": [v(32.53, -38.42) * mm, v(32.53, -38.65) * mm, v(32.51, -38.88) * mm, v(32.48, -39.1) * mm]});
            skFitSpline(sketch, "E310", {"points": [v(32.48, -39.1) * mm, v(32.48, -39.3) * mm, v(32.46, -39.5) * mm, v(32.42, -39.74) * mm]});
            skFitSpline(sketch, "E311", {"points": [v(32.42, -39.74) * mm, v(32.8, -39.7) * mm, v(33.16, -39.68) * mm, v(33.5, -39.68) * mm]});
            skFitSpline(sketch, "E312", {"points": [v(33.5, -39.68) * mm, v(33.85, -39.64) * mm, v(34.17, -39.62) * mm, v(34.48, -39.62) * mm]});
            skLineSegment(sketch, "E313", {"start": v(40.7, -29.05) * mm, "end": v(35.96, -31.05) * mm});
            skLineSegment(sketch, "E314", {"start": v(35.96, -31.05) * mm, "end": v(40.7, -29.05) * mm});
            skFitSpline(sketch, "E315", {"points": [v(36.3, -39.62) * mm, v(36.3, -41.76) * mm, v(36.29, -43.7) * mm, v(36.25, -45.45) * mm]});
            skFitSpline(sketch, "E316", {"points": [v(36.25, -45.45) * mm, v(36.2, -47.17) * mm, v(36.15, -48.75) * mm, v(36.08, -50.2) * mm]});
            skFitSpline(sketch, "E317", {"points": [v(36.08, -50.2) * mm, v(36.04, -51.6) * mm, v(36, -52.92) * mm, v(35.96, -54.14) * mm]});
            skFitSpline(sketch, "E318", {"points": [v(35.96, -54.14) * mm, v(35.92, -55.32) * mm, v(35.9, -56.42) * mm, v(35.9, -57.45) * mm]});
            skFitSpline(sketch, "E319", {"points": [v(35.9, -57.45) * mm, v(35.9, -59.74) * mm, v(36.48, -61.47) * mm, v(37.62, -62.65) * mm]});
            skFitSpline(sketch, "E320", {"points": [v(37.62, -62.65) * mm, v(38.76, -63.83) * mm, v(40.53, -64.42) * mm, v(42.93, -64.42) * mm]});
            skFitSpline(sketch, "E321", {"points": [v(42.93, -64.42) * mm, v(43.66, -64.42) * mm, v(44.4, -64.33) * mm, v(45.16, -64.14) * mm]});
            skFitSpline(sketch, "E322", {"points": [v(45.16, -64.14) * mm, v(45.96, -63.99) * mm, v(46.69, -63.85) * mm, v(47.33, -63.74) * mm]});
            skLineSegment(sketch, "E323", {"start": v(34.48, -39.62) * mm, "end": v(36.3, -39.62) * mm});
            skLineSegment(sketch, "E324", {"start": v(36.3, -39.62) * mm, "end": v(34.48, -39.62) * mm});
            skFitSpline(sketch, "E325", {"points": [v(47.33, -62.37) * mm, v(46.95, -62.48) * mm, v(46.5, -62.58) * mm, v(45.96, -62.65) * mm]});
            skFitSpline(sketch, "E326", {"points": [v(45.96, -62.65) * mm, v(45.47, -62.73) * mm, v(45.07, -62.77) * mm, v(44.76, -62.77) * mm]});
            skFitSpline(sketch, "E327", {"points": [v(44.76, -62.77) * mm, v(43.62, -62.77) * mm, v(42.74, -62.52) * mm, v(42.13, -62.02) * mm]});
            skFitSpline(sketch, "E328", {"points": [v(42.13, -62.02) * mm, v(41.52, -61.53) * mm, v(41.07, -60.88) * mm, v(40.76, -60.08) * mm]});
            skFitSpline(sketch, "E329", {"points": [v(40.76, -60.08) * mm, v(40.46, -59.24) * mm, v(40.27, -58.3) * mm, v(40.2, -57.28) * mm]});
            skFitSpline(sketch, "E330", {"points": [v(40.2, -57.28) * mm, v(40.15, -56.25) * mm, v(40.13, -55.2) * mm, v(40.13, -54.14) * mm]});
            skFitSpline(sketch, "E331", {"points": [v(40.13, -54.14) * mm, v(40.13, -52.88) * mm, v(40.13, -51.45) * mm, v(40.13, -49.85) * mm]});
            skFitSpline(sketch, "E332", {"points": [v(40.13, -49.85) * mm, v(40.17, -48.25) * mm, v(40.2, -46.73) * mm, v(40.25, -45.28) * mm]});
            skFitSpline(sketch, "E333", {"points": [v(40.25, -45.28) * mm, v(40.29, -43.8) * mm, v(40.32, -42.52) * mm, v(40.36, -41.45) * mm]});
            skFitSpline(sketch, "E334", {"points": [v(40.36, -41.45) * mm, v(40.44, -40.39) * mm, v(40.5, -39.78) * mm, v(40.53, -39.62) * mm]});
            skLineSegment(sketch, "E335", {"start": v(47.33, -63.74) * mm, "end": v(47.33, -62.37) * mm});
            skLineSegment(sketch, "E336", {"start": v(47.33, -62.37) * mm, "end": v(47.33, -63.74) * mm});
            skFitSpline(sketch, "E337", {"points": [v(43.33, -39.62) * mm, v(43.94, -39.62) * mm, v(44.51, -39.64) * mm, v(45.05, -39.68) * mm]});
            skFitSpline(sketch, "E338", {"points": [v(45.05, -39.68) * mm, v(45.58, -39.68) * mm, v(46.1, -39.7) * mm, v(46.6, -39.74) * mm]});
            skFitSpline(sketch, "E339", {"points": [v(46.6, -39.74) * mm, v(46.55, -39.62) * mm, v(46.53, -39.43) * mm, v(46.53, -39.17) * mm]});
            skLineSegment(sketch, "E340", {"start": v(40.53, -39.62) * mm, "end": v(43.33, -39.62) * mm});
            skLineSegment(sketch, "E341", {"start": v(43.33, -39.62) * mm, "end": v(40.53, -39.62) * mm});
            skFitSpline(sketch, "E342", {"points": [v(46.53, -37.97) * mm, v(46.53, -37.66) * mm, v(46.55, -37.45) * mm, v(46.6, -37.34) * mm]});
            skFitSpline(sketch, "E343", {"points": [v(46.6, -37.34) * mm, v(45.26, -37.41) * mm, v(44.02, -37.47) * mm, v(42.88, -37.5) * mm]});
            skFitSpline(sketch, "E344", {"points": [v(42.88, -37.5) * mm, v(41.73, -37.5) * mm, v(40.95, -37.5) * mm, v(40.53, -37.5) * mm]});
            skFitSpline(sketch, "E345", {"points": [v(40.53, -37.5) * mm, v(40.6, -36.1) * mm, v(40.67, -34.7) * mm, v(40.7, -33.34) * mm]});
            skFitSpline(sketch, "E346", {"points": [v(40.7, -33.34) * mm, v(40.78, -31.93) * mm, v(40.88, -30.5) * mm, v(41, -29.05) * mm]});
            skLineSegment(sketch, "E347", {"start": v(46.53, -39.17) * mm, "end": v(46.53, -38.54) * mm});
            skLineSegment(sketch, "E348", {"start": v(46.53, -38.54) * mm, "end": v(46.53, -37.97) * mm});
            skLineSegment(sketch, "E349", {"start": v(46.53, -37.97) * mm, "end": v(46.53, -39.17) * mm});
            skFitSpline(sketch, "E350", {"points": [v(-20, -54) * mm, v(-20, -56.98) * mm, v(-19.15, -59.26) * mm, v(-17.48, -60.86) * mm]});
            skFitSpline(sketch, "E351", {"points": [v(-17.48, -60.86) * mm, v(-15.76, -62.43) * mm, v(-13.42, -63.2) * mm, v(-10.45, -63.2) * mm]});
            skFitSpline(sketch, "E352", {"points": [v(-10.45, -63.2) * mm, v(-8.62, -63.2) * mm, v(-6.92, -62.79) * mm, v(-5.36, -61.95) * mm]});
            skFitSpline(sketch, "E353", {"points": [v(-5.36, -61.95) * mm, v(-3.8, -61.07) * mm, v(-2.52, -59.72) * mm, v(-1.53, -57.9) * mm]});
            skLineSegment(sketch, "E354", {"start": v(41, -29.05) * mm, "end": v(40.7, -29.05) * mm});
            skLineSegment(sketch, "E355", {"start": v(40.7, -29.05) * mm, "end": v(41, -29.05) * mm});
            skFitSpline(sketch, "E356", {"points": [v(-1.42, -60.35) * mm, v(-1.42, -60.77) * mm, v(-1.44, -61.17) * mm, v(-1.48, -61.55) * mm]});
            skFitSpline(sketch, "E357", {"points": [v(-1.48, -61.55) * mm, v(-1.48, -61.93) * mm, v(-1.5, -62.3) * mm, v(-1.53, -62.64) * mm]});
            skFitSpline(sketch, "E358", {"points": [v(-1.53, -62.64) * mm, v(-0.77, -62.56) * mm, v(-0.03, -62.52) * mm, v(0.7, -62.52) * mm]});
            skFitSpline(sketch, "E359", {"points": [v(0.7, -62.52) * mm, v(1.42, -62.52) * mm, v(2.16, -62.56) * mm, v(2.92, -62.64) * mm]});
            skFitSpline(sketch, "E360", {"points": [v(2.92, -62.64) * mm, v(2.85, -61.11) * mm, v(2.8, -59.53) * mm, v(2.75, -57.9) * mm]});
            skFitSpline(sketch, "E361", {"points": [v(2.75, -57.9) * mm, v(2.71, -56.26) * mm, v(2.7, -54.58) * mm, v(2.7, -52.86) * mm]});
            skFitSpline(sketch, "E362", {"points": [v(2.7, -52.86) * mm, v(2.7, -49.78) * mm, v(2.71, -46.86) * mm, v(2.75, -44.12) * mm]});
            skFitSpline(sketch, "E363", {"points": [v(2.75, -44.12) * mm, v(2.8, -41.34) * mm, v(2.9, -38.46) * mm, v(3.1, -35.5) * mm]});
            skFitSpline(sketch, "E364", {"points": [v(3.1, -35.5) * mm, v(2.71, -35.57) * mm, v(2.33, -35.65) * mm, v(1.95, -35.72) * mm]});
            skFitSpline(sketch, "E365", {"points": [v(1.95, -35.72) * mm, v(1.57, -35.76) * mm, v(1.17, -35.78) * mm, v(0.75, -35.78) * mm]});
            skFitSpline(sketch, "E366", {"points": [v(0.75, -35.78) * mm, v(0.33, -35.78) * mm, v(-0.07, -35.76) * mm, v(-0.45, -35.72) * mm]});
            skFitSpline(sketch, "E367", {"points": [v(-0.45, -35.72) * mm, v(-0.83, -35.65) * mm, v(-1.23, -35.57) * mm, v(-1.65, -35.5) * mm]});
            skFitSpline(sketch, "E368", {"points": [v(-1.65, -35.5) * mm, v(-1.6, -36.18) * mm, v(-1.6, -36.9) * mm, v(-1.6, -37.66) * mm]});
            skFitSpline(sketch, "E369", {"points": [v(-1.6, -37.66) * mm, v(-1.55, -38.43) * mm, v(-1.53, -39.23) * mm, v(-1.53, -40.06) * mm]});
            skLineSegment(sketch, "E370", {"start": v(-1.53, -57.9) * mm, "end": v(-1.42, -57.9) * mm});
            skLineSegment(sketch, "E371", {"start": v(-1.42, -57.9) * mm, "end": v(-1.42, -60.35) * mm});
            skLineSegment(sketch, "E372", {"start": v(-1.42, -60.35) * mm, "end": v(-1.53, -57.9) * mm});
            skFitSpline(sketch, "E373", {"points": [v(-1.53, -44.86) * mm, v(-1.53, -47.11) * mm, v(-1.55, -48.88) * mm, v(-1.6, -50.18) * mm]});
            skFitSpline(sketch, "E374", {"points": [v(-1.6, -50.18) * mm, v(-1.6, -51.47) * mm, v(-1.65, -52.5) * mm, v(-1.76, -53.26) * mm]});
            skFitSpline(sketch, "E375", {"points": [v(-1.76, -53.26) * mm, v(-1.84, -54.03) * mm, v(-1.95, -54.64) * mm, v(-2.1, -55.1) * mm]});
            skFitSpline(sketch, "E376", {"points": [v(-2.1, -55.1) * mm, v(-2.26, -55.55) * mm, v(-2.47, -56.1) * mm, v(-2.73, -56.75) * mm]});
            skFitSpline(sketch, "E377", {"points": [v(-2.73, -56.75) * mm, v(-3.23, -57.78) * mm, v(-4, -58.66) * mm, v(-5.08, -59.38) * mm]});
            skFitSpline(sketch, "E378", {"points": [v(-5.08, -59.38) * mm, v(-6.14, -60.06) * mm, v(-7.48, -60.4) * mm, v(-9.08, -60.4) * mm]});
            skFitSpline(sketch, "E379", {"points": [v(-9.08, -60.4) * mm, v(-10.18, -60.4) * mm, v(-11.15, -60.22) * mm, v(-12, -59.84) * mm]});
            skFitSpline(sketch, "E380", {"points": [v(-12, -59.84) * mm, v(-12.8, -59.42) * mm, v(-13.46, -58.9) * mm, v(-14, -58.3) * mm]});
            skFitSpline(sketch, "E381", {"points": [v(-14, -58.3) * mm, v(-14.49, -57.76) * mm, v(-14.9, -56.98) * mm, v(-15.25, -55.95) * mm]});
            skFitSpline(sketch, "E382", {"points": [v(-15.25, -55.95) * mm, v(-15.6, -54.88) * mm, v(-15.76, -53.36) * mm, v(-15.76, -51.38) * mm]});
            skFitSpline(sketch, "E383", {"points": [v(-15.76, -51.38) * mm, v(-15.76, -48.52) * mm, v(-15.72, -45.74) * mm, v(-15.65, -43.04) * mm]});
            skFitSpline(sketch, "E384", {"points": [v(-15.65, -43.04) * mm, v(-15.53, -40.3) * mm, v(-15.38, -37.78) * mm, v(-15.2, -35.5) * mm]});
            skFitSpline(sketch, "E385", {"points": [v(-15.2, -35.5) * mm, v(-16.14, -35.68) * mm, v(-16.92, -35.78) * mm, v(-17.53, -35.78) * mm]});
            skFitSpline(sketch, "E386", {"points": [v(-17.53, -35.78) * mm, v(-18.18, -35.78) * mm, v(-18.98, -35.68) * mm, v(-19.93, -35.5) * mm]});
            skFitSpline(sketch, "E387", {"points": [v(-19.93, -35.5) * mm, v(-19.9, -37.1) * mm, v(-19.88, -38.67) * mm, v(-19.88, -40.24) * mm]});
            skFitSpline(sketch, "E388", {"points": [v(-19.88, -40.24) * mm, v(-19.84, -41.8) * mm, v(-19.82, -43.25) * mm, v(-19.82, -44.58) * mm]});
            skFitSpline(sketch, "E389", {"points": [v(-19.82, -44.58) * mm, v(-19.82, -45.99) * mm, v(-19.86, -47.42) * mm, v(-19.93, -48.86) * mm]});
            skFitSpline(sketch, "E390", {"points": [v(-19.93, -48.86) * mm, v(-19.97, -50.27) * mm, v(-20, -51.99) * mm, v(-20, -54) * mm]});
            skLineSegment(sketch, "E391", {"start": v(-1.53, -40.06) * mm, "end": v(-1.53, -44.86) * mm});
            skLineSegment(sketch, "E392", {"start": v(-1.53, -44.86) * mm, "end": v(-1.53, -40.06) * mm});
            skFitSpline(sketch, "E393", {"points": [v(24.8, -40.23) * mm, v(24.8, -39.47) * mm, v(24.82, -38.63) * mm, v(24.86, -37.72) * mm]});
            skFitSpline(sketch, "E394", {"points": [v(24.86, -37.72) * mm, v(24.9, -36.76) * mm, v(25.01, -36.06) * mm, v(25.2, -35.6) * mm]});
            skFitSpline(sketch, "E395", {"points": [v(25.2, -35.6) * mm, v(24.82, -35.45) * mm, v(24.5, -35.35) * mm, v(24.23, -35.32) * mm]});
            skFitSpline(sketch, "E396", {"points": [v(24.23, -35.32) * mm, v(24, -35.28) * mm, v(23.72, -35.26) * mm, v(23.37, -35.26) * mm]});
            skFitSpline(sketch, "E397", {"points": [v(23.37, -35.26) * mm, v(20.6, -35.26) * mm, v(18.08, -37.32) * mm, v(15.83, -41.43) * mm]});
            skLineSegment(sketch, "E398", {"start": v(24.4, -40.52) * mm, "end": v(24.8, -40.23) * mm});
            skLineSegment(sketch, "E399", {"start": v(24.8, -40.23) * mm, "end": v(24.4, -40.52) * mm});
            skFitSpline(sketch, "E400", {"points": [v(15.72, -41.37) * mm, v(15.72, -40.65) * mm, v(15.72, -39.89) * mm, v(15.72, -39.09) * mm]});
            skFitSpline(sketch, "E401", {"points": [v(15.72, -39.09) * mm, v(15.75, -38.29) * mm, v(15.85, -37.2) * mm, v(16, -35.83) * mm]});
            skFitSpline(sketch, "E402", {"points": [v(16, -35.83) * mm, v(15.58, -35.9) * mm, v(15.18, -35.98) * mm, v(14.8, -36.06) * mm]});
            skFitSpline(sketch, "E403", {"points": [v(14.8, -36.06) * mm, v(14.42, -36.1) * mm, v(14.06, -36.12) * mm, v(13.72, -36.12) * mm]});
            skFitSpline(sketch, "E404", {"points": [v(13.72, -36.12) * mm, v(13.3, -36.12) * mm, v(12.9, -36.1) * mm, v(12.52, -36.06) * mm]});
            skFitSpline(sketch, "E405", {"points": [v(12.52, -36.06) * mm, v(12.13, -35.98) * mm, v(11.73, -35.9) * mm, v(11.32, -35.83) * mm]});
            skFitSpline(sketch, "E406", {"points": [v(11.32, -35.83) * mm, v(11.43, -38.35) * mm, v(11.49, -40.57) * mm, v(11.49, -42.52) * mm]});
            skFitSpline(sketch, "E407", {"points": [v(11.49, -42.52) * mm, v(11.53, -44.46) * mm, v(11.54, -46.17) * mm, v(11.54, -47.66) * mm]});
            skLineSegment(sketch, "E408", {"start": v(15.83, -41.43) * mm, "end": v(15.72, -41.37) * mm});
            skLineSegment(sketch, "E409", {"start": v(15.72, -41.37) * mm, "end": v(15.83, -41.43) * mm});
            skFitSpline(sketch, "E410", {"points": [v(11.54, -49.49) * mm, v(11.54, -52.73) * mm, v(11.53, -55.47) * mm, v(11.49, -57.72) * mm]});
            skFitSpline(sketch, "E411", {"points": [v(11.49, -57.72) * mm, v(11.49, -59.93) * mm, v(11.43, -61.68) * mm, v(11.32, -62.97) * mm]});
            skFitSpline(sketch, "E412", {"points": [v(11.32, -62.97) * mm, v(12.08, -62.9) * mm, v(12.88, -62.86) * mm, v(13.72, -62.86) * mm]});
            skFitSpline(sketch, "E413", {"points": [v(13.72, -62.86) * mm, v(14.48, -62.86) * mm, v(15.24, -62.9) * mm, v(16, -62.97) * mm]});
            skFitSpline(sketch, "E414", {"points": [v(16, -62.97) * mm, v(15.89, -62.14) * mm, v(15.81, -61.05) * mm, v(15.77, -59.72) * mm]});
            skFitSpline(sketch, "E415", {"points": [v(15.77, -59.72) * mm, v(15.77, -58.35) * mm, v(15.77, -56.38) * mm, v(15.77, -53.83) * mm]});
            skLineSegment(sketch, "E416", {"start": v(11.54, -47.66) * mm, "end": v(11.54, -49.49) * mm});
            skLineSegment(sketch, "E417", {"start": v(11.54, -49.49) * mm, "end": v(11.54, -47.66) * mm});
            skFitSpline(sketch, "E418", {"points": [v(15.77, -47.55) * mm, v(15.77, -46.44) * mm, v(15.9, -45.41) * mm, v(16.17, -44.46) * mm]});
            skFitSpline(sketch, "E419", {"points": [v(16.17, -44.46) * mm, v(16.44, -43.47) * mm, v(16.82, -42.63) * mm, v(17.32, -41.95) * mm]});
            skFitSpline(sketch, "E420", {"points": [v(17.32, -41.95) * mm, v(17.81, -41.22) * mm, v(18.42, -40.65) * mm, v(19.14, -40.23) * mm]});
            skFitSpline(sketch, "E421", {"points": [v(19.14, -40.23) * mm, v(19.87, -39.81) * mm, v(20.69, -39.6) * mm, v(21.6, -39.6) * mm]});
            skFitSpline(sketch, "E422", {"points": [v(21.6, -39.6) * mm, v(22.17, -39.6) * mm, v(22.73, -39.7) * mm, v(23.26, -39.89) * mm]});
            skFitSpline(sketch, "E423", {"points": [v(23.26, -39.89) * mm, v(23.83, -40.08) * mm, v(24.21, -40.29) * mm, v(24.4, -40.52) * mm]});
            skLineSegment(sketch, "E424", {"start": v(15.77, -53.83) * mm, "end": v(15.77, -47.55) * mm});
            skLineSegment(sketch, "E425", {"start": v(15.77, -47.55) * mm, "end": v(15.77, -53.83) * mm});
            skSolve(sketch);
        }
        {
            var Q0;
            Q0=makeQuery(id+"F0.imprint","IMPRINT",FACE,{"disambiguationData":[TD([[makeQuery(id+"F0.imprint","IMPRINT",EDGE,{"derivedFrom":sQuery(id+"F0.wireOp",EDGE,"E0")}),-1.0]])]});
            var Q1;
            Q1=makeQuery(id+"F0.imprint","IMPRINT",FACE,{"disambiguationData":[TD([[makeQuery(id+"F0.imprint","IMPRINT",EDGE,{"derivedFrom":sQuery(id+"F0.wireOp",EDGE,"E82")}),1.0]])]});
            var Q2;
            Q2=makeQuery(id+"F0.imprint","IMPRINT",FACE,{"disambiguationData":[TD([[makeQuery(id+"F0.imprint","IMPRINT",EDGE,{"derivedFrom":sQuery(id+"F0.wireOp",EDGE,"E174")}),1.0]])]});
            var Q3;
            Q3=makeQuery(id+"F0.imprint","IMPRINT",FACE,{"disambiguationData":[TD([[makeQuery(id+"F0.imprint","IMPRINT",EDGE,{"derivedFrom":sQuery(id+"F0.wireOp",EDGE,"E123")}),1.0]])]});
            var Q4;
            Q4=makeQuery(id+"F0.imprint","IMPRINT",FACE,{"disambiguationData":[TD([[makeQuery(id+"F0.imprint","IMPRINT",EDGE,{"derivedFrom":sQuery(id+"F0.wireOp",EDGE,"E33")}),1.0]])]});
            var Q5;
            Q5=makeQuery(id+"F0.imprint","IMPRINT",FACE,{"disambiguationData":[TD([[makeQuery(id+"F0.imprint","IMPRINT",EDGE,{"derivedFrom":sQuery(id+"F0.wireOp",EDGE,"E304")}),1.0]])]});
            var Q6;
            Q6=makeQuery(id+"F0.imprint","IMPRINT",FACE,{"disambiguationData":[TD([[makeQuery(id+"F0.imprint","IMPRINT",EDGE,{"derivedFrom":sQuery(id+"F0.wireOp",EDGE,"E393")}),1.0]])]});
            var Q7;
            Q7=makeQuery(id+"F0.imprint","IMPRINT",FACE,{"disambiguationData":[TD([[makeQuery(id+"F0.imprint","IMPRINT",EDGE,{"derivedFrom":sQuery(id+"F0.wireOp",EDGE,"E350")}),1.0]])]});
            var Q8;
            Q8=makeQuery(id+"F0.imprint","IMPRINT",FACE,{"disambiguationData":[TD([[makeQuery(id+"F0.imprint","IMPRINT",EDGE,{"derivedFrom":sQuery(id+"F0.wireOp",EDGE,"E255")}),1.0]])]});
            var Q9;
            Q9=makeQuery(id+"F0.imprint","IMPRINT",FACE,{"disambiguationData":[TD([[makeQuery(id+"F0.imprint","IMPRINT",EDGE,{"derivedFrom":sQuery(id+"F0.wireOp",EDGE,"E215")}),1.0]])]});
            extrude(context, id + "F1", {"entities" : qUnion([Q0, Q1, Q2, Q3, Q4, Q5, Q6, Q7, Q8, Q9]), "depth" : 2 * mm, "offsetDistance" : 25 * mm});
        }
    });
